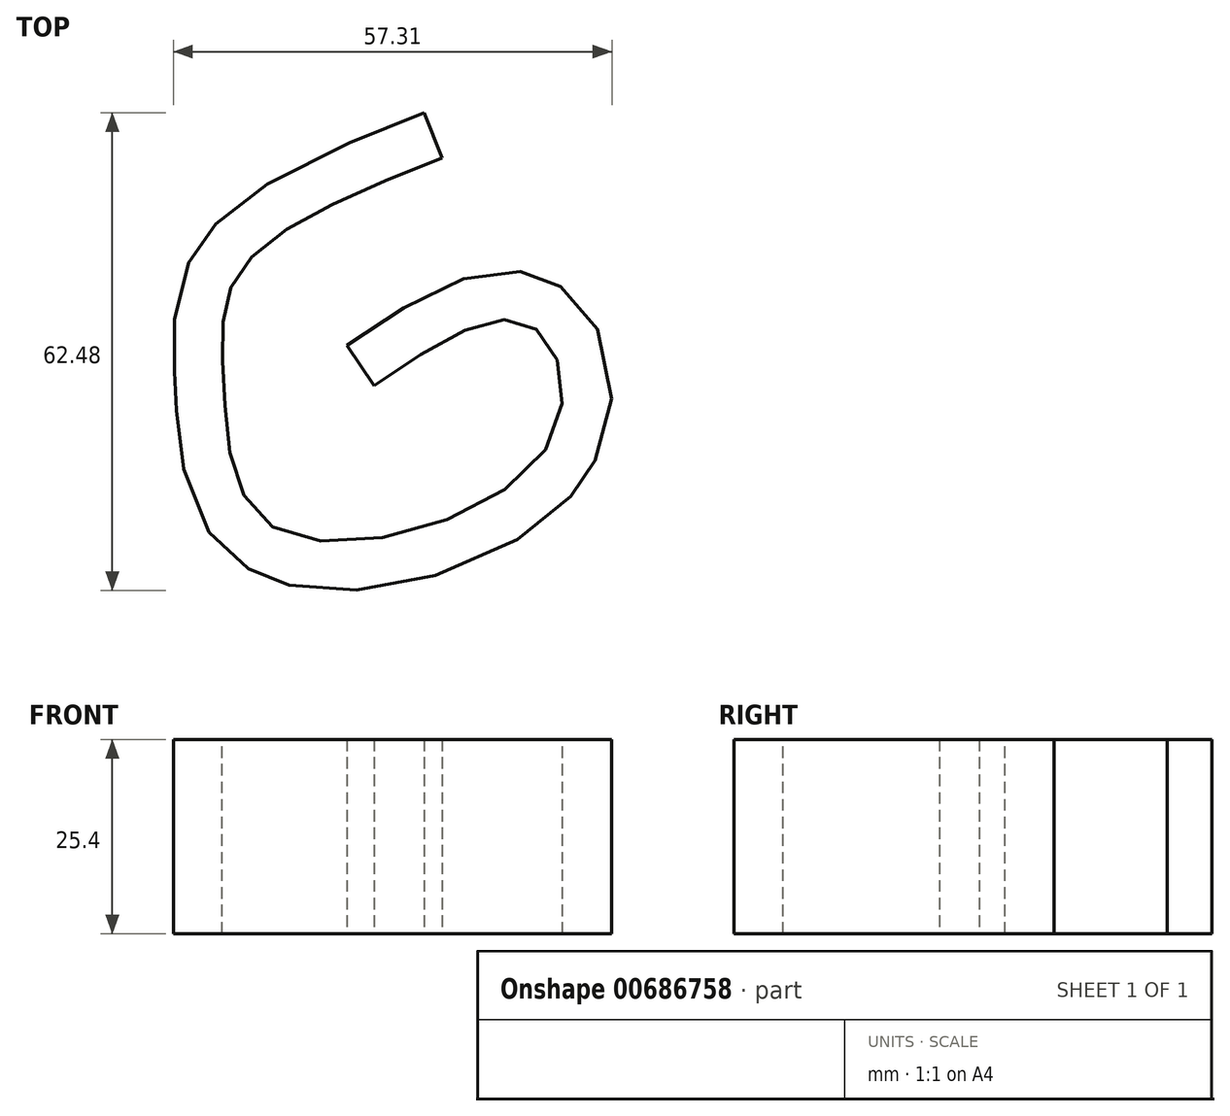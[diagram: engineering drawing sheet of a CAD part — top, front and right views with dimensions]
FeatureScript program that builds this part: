
annotation { "Feature Type Name" : "Feature", "Feature Type Description" : "" }
export const myFeature = defineFeature(function(context is Context, id is Id, definition is map)
    precondition{}
    {
        {
            var Q0;
            Q0=qCreatedBy(makeId("Top.planeOp"),FACE);
            var sketch = newSketch(context, id + "F0", { "sketchPlane" : qUnion([Q0])});
            skFitSpline(sketch, "E0", {"points": [v(-111.23, 51.35) * mm, v(-137.37, 36.92) * mm, v(-139.76, 21.84) * mm, v(-132.55, 2.68) * mm, v(-97.73, 13.16) * mm, v(-99.84, 29.56) * mm, v(-120.1, 21.57) * mm], "startDerivative": vector(-172.13, -68.25) * mm, "endDerivative": vector(-141.96, -96.3) * mm});
            skFitSpline(sketch, "E1.0", {"points": [v(-113.57, 57.25) * mm, v(-115.36, 56.54) * mm, v(-118.98, 55.1) * mm, v(-124.34, 52.87) * mm, v(-129.48, 50.5) * mm, v(-133.46, 48.33) * mm, v(-136.41, 46.4) * mm, v(-138.5, 44.84) * mm, v(-140.1, 43.4) * mm, v(-141.3, 42.15) * mm, v(-142.16, 41.14) * mm, v(-142.95, 40.06) * mm, v(-143.64, 38.95) * mm, v(-144.25, 37.82) * mm, v(-144.93, 36.27) * mm, v(-145.56, 34.33) * mm, v(-146.02, 32.03) * mm, v(-146.25, 29.8) * mm, v(-146.32, 27.64) * mm, v(-146.3, 25.88) * mm, v(-146.25, 24.49) * mm, v(-146.2, 23.45) * mm, v(-146.15, 22.58) * mm, v(-146.12, 21.9) * mm, v(-146.08, 21.2) * mm, v(-146.04, 20.3) * mm, v(-145.98, 19.19) * mm, v(-145.91, 18.02) * mm, v(-145.8, 16.43) * mm, v(-145.6, 14.35) * mm, v(-145.23, 11.78) * mm, v(-144.65, 9.13) * mm, v(-143.79, 6.45) * mm, v(-142.54, 3.77) * mm, v(-141.09, 1.6) * mm, v(-139.63, 0) * mm, v(-138.38, -1.12) * mm, v(-137.23, -1.95) * mm, v(-136.25, -2.55) * mm, v(-135.48, -2.97) * mm, v(-134.69, -3.34) * mm, v(-133.62, -3.78) * mm, v(-132.27, -4.23) * mm, v(-130.62, -4.64) * mm, v(-128.4, -5.02) * mm, v(-125.57, -5.23) * mm, v(-122.1, -5.13) * mm, v(-118.6, -4.73) * mm, v(-115.07, -4.04) * mm, v(-110.4, -2.77) * mm, v(-105.85, -0.99) * mm, v(-101.6, 1.29) * mm, v(-98.61, 3.26) * mm, v(-96.32, 5.15) * mm, v(-94.65, 6.82) * mm, v(-93.67, 7.95) * mm, v(-92.95, 8.9) * mm, v(-92.43, 9.65) * mm, v(-91.94, 10.41) * mm, v(-91.35, 11.44) * mm, v(-90.72, 12.76) * mm, v(-89.9, 14.9) * mm, v(-89.25, 17.6) * mm, v(-89.01, 20.8) * mm, v(-89.28, 23.9) * mm, v(-90.01, 26.84) * mm, v(-91.21, 29.6) * mm, v(-92.63, 31.7) * mm, v(-94.07, 33.21) * mm, v(-95.1, 34.07) * mm, v(-96, 34.69) * mm, v(-96.73, 35.1) * mm, v(-97.5, 35.48) * mm, v(-98.53, 35.9) * mm, v(-99.85, 36.28) * mm, v(-101.41, 36.51) * mm, v(-102.93, 36.56) * mm, v(-104.88, 36.42) * mm, v(-107.15, 35.95) * mm, v(-109.7, 35.07) * mm, v(-112.14, 33.97) * mm, v(-114.51, 32.71) * mm, v(-116.85, 31.33) * mm, v(-119.93, 29.37) * mm, v(-122.2, 27.83) * mm, v(-123.67, 26.83) * mm]});
            skLineSegment(sketch, "E2", {"start": v(-111.23, 51.35) * mm, "end": v(-113.57, 57.25) * mm});
            skLineSegment(sketch, "E3", {"start": v(-120.1, 21.57) * mm, "end": v(-123.67, 26.83) * mm});
            skSolve(sketch);
        }
        {
            var Q0;
            Q0 = qSketchRegion(id + "F0", true);
            extrude(context, id + "F1", {"entities" : qUnion([Q0]), "depth" : 25.4 * mm, "offsetDistance" : 25.4 * mm});
        }
        {
            var Q0;
            Q0=sQuery(id+"F0.wireOp",EDGE,"E0");
            extrude(context, id + "F2", {"bodyType" : ToolBodyType.SURFACE, "surfaceEntities" : qUnion([Q0]), "depth" : 25.4 * mm, "offsetDistance" : 25.4 * mm});
        }
    });
